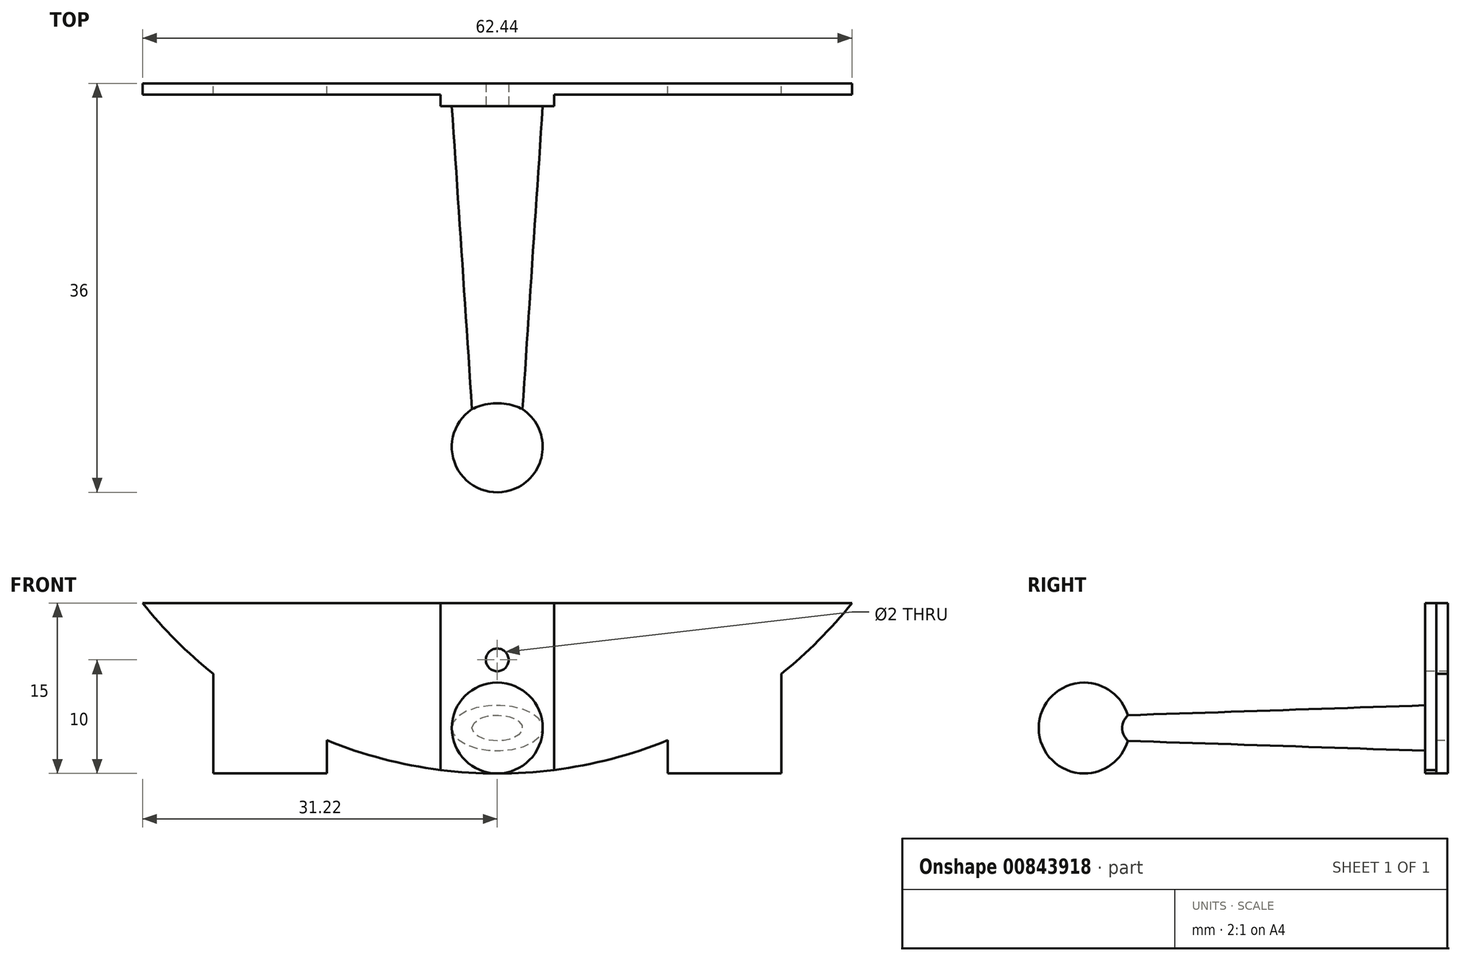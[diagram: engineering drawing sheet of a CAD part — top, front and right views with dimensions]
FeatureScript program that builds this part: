
annotation { "Feature Type Name" : "Feature", "Feature Type Description" : "" }
export const myFeature = defineFeature(function(context is Context, id is Id, definition is map)
    precondition{}
    {
        {
            var Q0;
            Q0=qCreatedBy(makeId("Front.planeOp"),FACE);
            var sketch = newSketch(context, id + "F0", { "sketchPlane" : qUnion([Q0])});
            skArc(sketch, "E0", {"start": v(-31.22, -25) * mm, "mid": v(-28.28, -28.28) * mm, "end": v(-25, -31.22) * mm});
            skLineSegment(sketch, "E1", {"start": v(-31.22, -25) * mm, "end": v(31.22, -25) * mm});
            skLineSegment(sketch, "E2.top", {"start": v(15, -40) * mm, "end": v(25, -40) * mm});
            skLineSegment(sketch, "E2.left", {"start": v(15, -37.08) * mm, "end": v(15, -40) * mm});
            skLineSegment(sketch, "E2.right", {"start": v(25, -31.22) * mm, "end": v(25, -40) * mm});
            skArc(sketch, "E3.trimOffspring", {"start": v(25, -31.22) * mm, "mid": v(28.28, -28.28) * mm, "end": v(31.22, -25) * mm});
            skLineSegment(sketch, "E4.top", {"start": v(-25, -40) * mm, "end": v(-15, -40) * mm});
            skLineSegment(sketch, "E4.left", {"start": v(-25, -31.22) * mm, "end": v(-25, -40) * mm});
            skLineSegment(sketch, "E4.right", {"start": v(-15, -37.08) * mm, "end": v(-15, -40) * mm});
            skArc(sketch, "E5.trimOffspring", {"start": v(-15, -37.08) * mm, "mid": v(0, -40) * mm, "end": v(15, -37.08) * mm});
            skSolve(sketch);
        }
        {
            var Q0;
            Q0 = qSketchRegion(id + "F0", true);
            extrude(context, id + "F1", {"entities" : qUnion([Q0]), "depth" : 1 * mm, "offsetDistance" : 25 * mm});
        }
        {
            var Q0;
            Q0=makeQuery(id+"F1.opExtrude","CAP_FACE",FACE,{"disambiguationData":[OSD([sQuery(id+"F0.wireOp",EDGE,"E0"),sQuery(id+"F0.wireOp",EDGE,"E1"),sQuery(id+"F0.wireOp",EDGE,"E2.top"),sQuery(id+"F0.wireOp",EDGE,"E2.left"),sQuery(id+"F0.wireOp",EDGE,"E2.right"),sQuery(id+"F0.wireOp",EDGE,"E3.trimOffspring"),sQuery(id+"F0.wireOp",EDGE,"E4.top"),sQuery(id+"F0.wireOp",EDGE,"E4.left"),sQuery(id+"F0.wireOp",EDGE,"E4.right"),sQuery(id+"F0.wireOp",EDGE,"E5.trimOffspring")])],"isStart":false});
            var sketch = newSketch(context, id + "F2", { "sketchPlane" : qUnion([Q0])});
            skLineSegment(sketch, "E6.bottom", {"start": v(-5, -25) * mm, "end": v(5, -25) * mm});
            skLineSegment(sketch, "E6.left", {"start": v(-5, -25) * mm, "end": v(-5, -39.69) * mm});
            skLineSegment(sketch, "E6.right", {"start": v(5, -25) * mm, "end": v(5, -39.69) * mm});
            skArc(sketch, "E7", {"start": v(-5, -39.69) * mm, "mid": v(0, -40) * mm, "end": v(5, -39.69) * mm});
            skSolve(sketch);
        }
        {
            var Q0;
            Q0 = qSketchRegion(id + "F2", true);
            extrude(context, id + "F3", {"entities" : qUnion([Q0]), "operationType" : NewBodyOperationType.ADD, "depth" : 1 * mm, "offsetDistance" : 25 * mm});
        }
        {
            var Q0;
            Q0=makeQuery(id+"F3.opExtrude","CAP_FACE",FACE,{"disambiguationData":[OSD([sQuery(id+"F2.wireOp",EDGE,"E6.bottom"),sQuery(id+"F2.wireOp",EDGE,"E6.left"),sQuery(id+"F2.wireOp",EDGE,"E6.right"),sQuery(id+"F2.wireOp",EDGE,"E7")])],"isStart":false});
            var sketch = newSketch(context, id + "F4", { "sketchPlane" : qUnion([Q0])});
            skEllipse(sketch, "E8", {"center": v(0, -36) * mm, "majorRadius": 2 * mm, "minorRadius": 4 * mm, "majorAxis": v(0, 1)});
            skSolve(sketch);
        }
        {
            var Q0;
            Q0=qCreatedBy(makeId("Front.planeOp"),FACE);
            cPlane(context, id + "F5", {"entities" : qUnion([Q0]), "cplaneType" : CPlaneType.OFFSET, "offset" : 32 * mm, "width" : 150 * mm, "height" : 150 * mm});
        }
        {
            var Q0;
            Q0=qCreatedBy(id+"F5.planeOp",FACE);
            var sketch = newSketch(context, id + "F6", { "sketchPlane" : qUnion([Q0])});
            skEllipse(sketch, "E9", {"center": v(0, -36) * mm, "majorRadius": 2 * mm, "minorRadius": 1 * mm, "majorAxis": v(-1, 0)});
            skSolve(sketch);
        }
        {
            var Q1;
            Q1=makeQuery(id+"F4.imprint","IMPRINT",FACE,{"disambiguationData":[TD([[makeQuery(id+"F4.imprint","IMPRINT",EDGE,{"derivedFrom":sQuery(id+"F4.wireOp",EDGE,"E8")}),1.0]])]});
            var Q2;
            Q2=makeQuery(id+"F6.imprint","IMPRINT",FACE,{"disambiguationData":[TD([[makeQuery(id+"F6.imprint","IMPRINT",EDGE,{"derivedFrom":sQuery(id+"F6.wireOp",EDGE,"E9")}),1.0]])]});
            loft(context, id + "F7", {"operationType" : NewBodyOperationType.ADD, "sheetProfilesArray" : [{ "sheetProfileEntities" : qUnion([Q1]) }, { "sheetProfileEntities" : qUnion([Q2]) }]});
        }
        {
            var Q0;
            Q0=makeQuery(id+"F7.opLoft","CAP_FACE",FACE,{"disambiguationData":[OSD([makeQuery(id+"F6.imprint","IMPRINT",FACE,{"disambiguationData":[TD([[makeQuery(id+"F6.imprint","IMPRINT",EDGE,{"derivedFrom":sQuery(id+"F6.wireOp",EDGE,"E9")}),1.0]])]})])],"isStart":true});
            var sketch = newSketch(context, id + "F8", { "sketchPlane" : qUnion([Q0])});
            skLineSegment(sketch, "E10", {"start": v(0, -35) * mm, "end": v(0, -37) * mm, "construction": true});
            skArc(sketch, "E11", {"start": v(0, -40) * mm, "mid": v(4, -36) * mm, "end": v(0, -32) * mm});
            skLineSegment(sketch, "E12", {"start": v(0, -32) * mm, "end": v(0, -40) * mm});
            skSolve(sketch);
        }
        {
            var Q0;
            Q0 = qSketchRegion(id + "F8", true);
            var Q1;
            Q1=sQuery(id+"F8.wireOp",EDGE,"E12");
            revolve(context, id + "F9", {"operationType" : NewBodyOperationType.ADD, "surfaceOperationType" : NewSurfaceOperationType.NEW, "entities" : qUnion([Q0]), "axis" : qUnion([Q1]), "revolveType" : RevolveType.FULL});
        }
        {
            var Q0;
            Q0=makeQuery(id+"F3.opExtrude","CAP_FACE",FACE,{"disambiguationData":[OSD([sQuery(id+"F2.wireOp",EDGE,"E6.bottom"),sQuery(id+"F2.wireOp",EDGE,"E6.left"),sQuery(id+"F2.wireOp",EDGE,"E6.right"),sQuery(id+"F2.wireOp",EDGE,"E7")])],"isStart":false});
            var sketch = newSketch(context, id + "F10", { "sketchPlane" : qUnion([Q0])});
            skCircle(sketch, "E13", {"center": v(0, -30) * mm, "radius": 1 * mm});
            skSolve(sketch);
        }
        {
            var Q0;
            Q0 = qSketchRegion(id + "F10", true);
            extrude(context, id + "F11", {"entities" : qUnion([Q0]), "operationType" : NewBodyOperationType.REMOVE, "endBound" : BoundingType.THROUGH_ALL, "oppositeDirection" : true, "depth" : 25 * mm, "offsetDistance" : 25 * mm});
        }
    });
